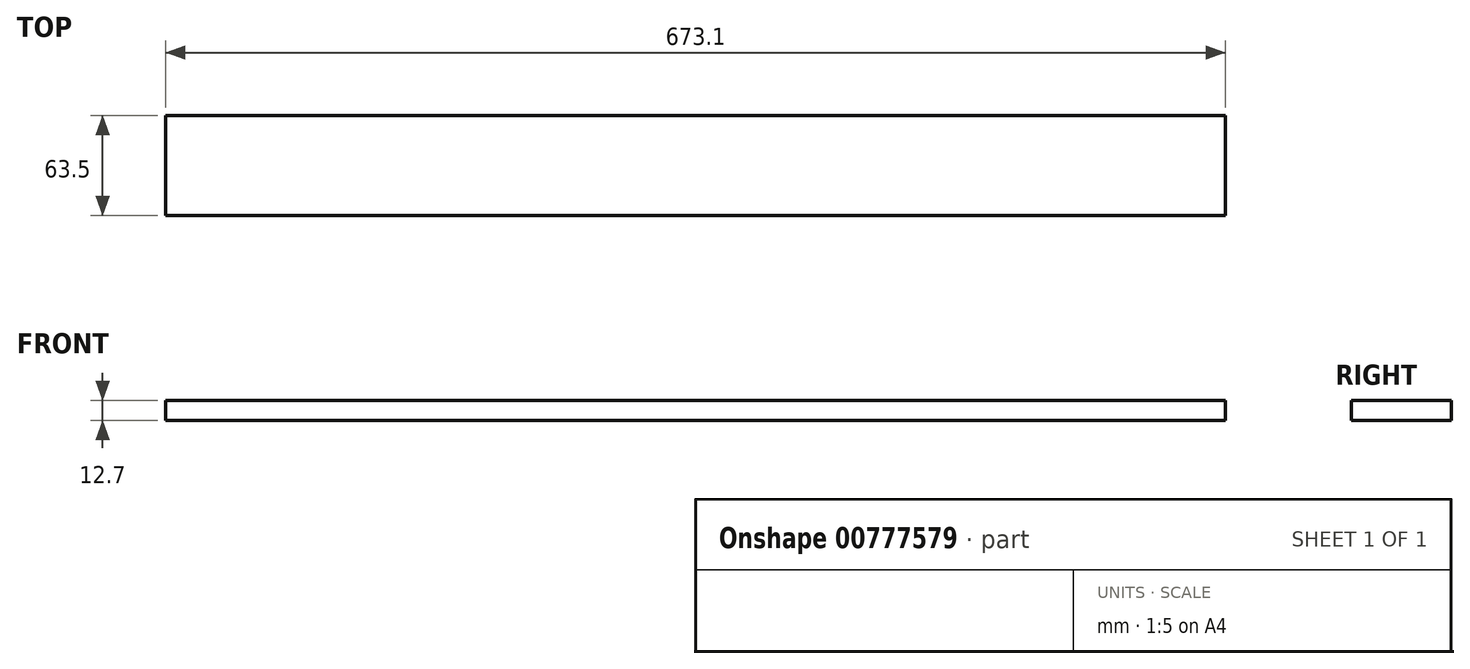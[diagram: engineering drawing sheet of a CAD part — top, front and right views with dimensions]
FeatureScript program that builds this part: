
annotation { "Feature Type Name" : "Feature", "Feature Type Description" : "" }
export const myFeature = defineFeature(function(context is Context, id is Id, definition is map)
    precondition{}
    {
        {
            var Q0;
            Q0=qCreatedBy(makeId("Top.planeOp"),FACE);
            var sketch = newSketch(context, id + "F0", { "sketchPlane" : qUnion([Q0])});
            skLineSegment(sketch, "E0.bottom", {"start": v(-673.1, 63.5) * mm, "end": v(0, 63.5) * mm});
            skLineSegment(sketch, "E0.top", {"start": v(-673.1, 0) * mm, "end": v(0, 0) * mm});
            skLineSegment(sketch, "E0.left", {"start": v(-673.1, 63.5) * mm, "end": v(-673.1, 0) * mm});
            skLineSegment(sketch, "E0.right", {"start": v(0, 63.5) * mm, "end": v(0, 0) * mm});
            skSolve(sketch);
        }
        {
            var Q0;
            Q0=makeQuery(id+"F0.imprint","IMPRINT",FACE,{"disambiguationData":[TD([[makeQuery(id+"F0.imprint","IMPRINT",EDGE,{"derivedFrom":sQuery(id+"F0.wireOp",EDGE,"E0.bottom")}),-1.0]])]});
            extrude(context, id + "F1", {"entities" : qUnion([Q0]), "depth" : 12.7 * mm});
        }
    });
